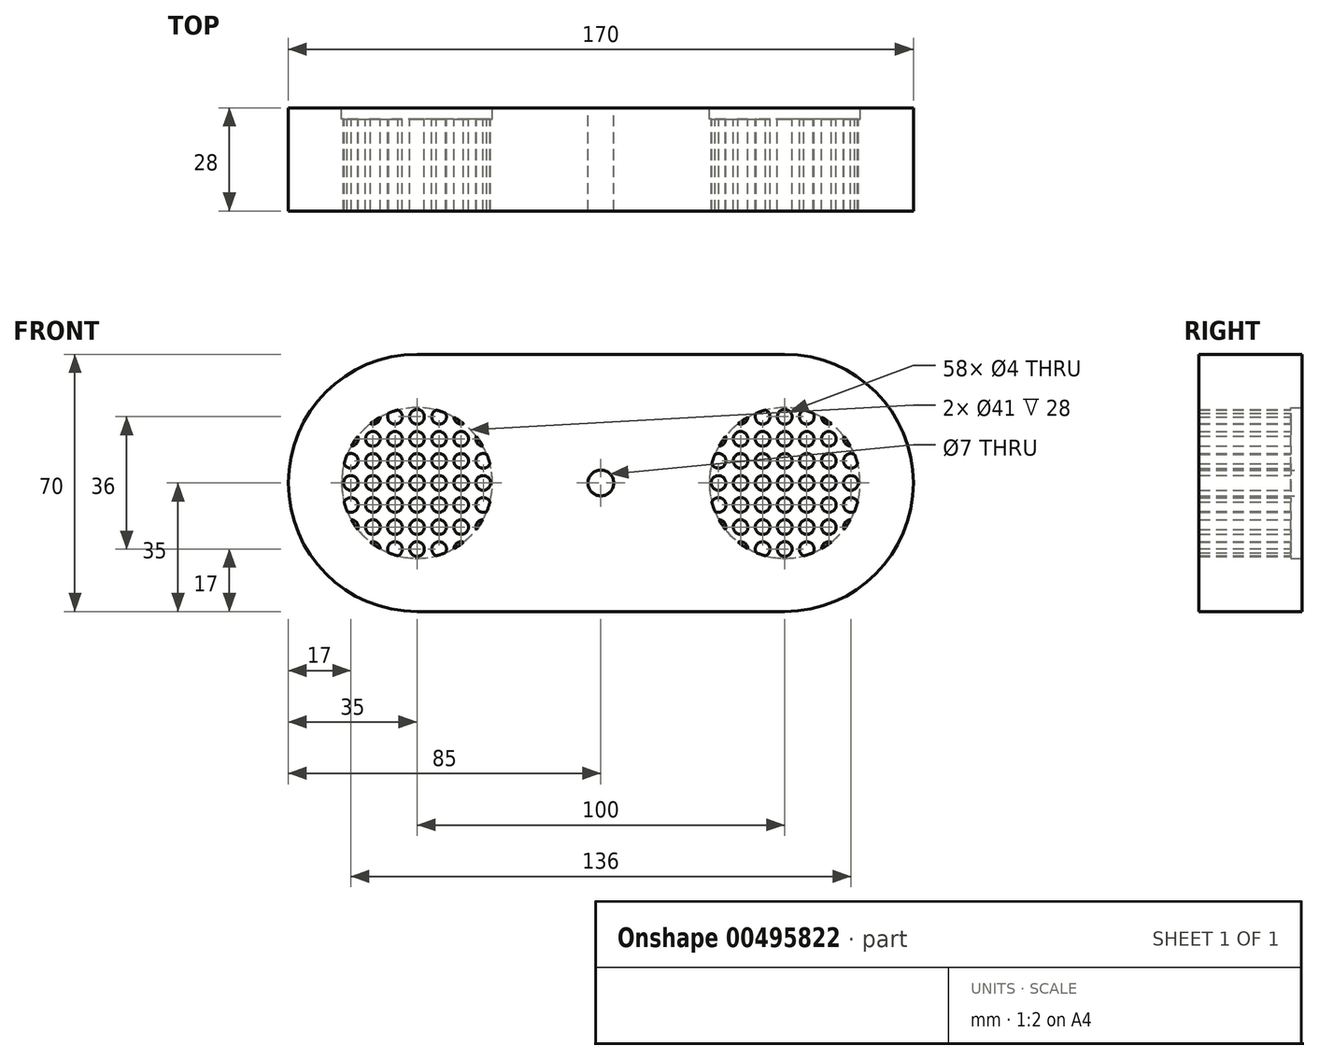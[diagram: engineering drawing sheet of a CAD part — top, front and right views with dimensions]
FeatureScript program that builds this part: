
annotation { "Feature Type Name" : "Feature", "Feature Type Description" : "" }
export const myFeature = defineFeature(function(context is Context, id is Id, definition is map)
    precondition{}
    {
        {
            var Q0;
            Q0=qCreatedBy(makeId("Front.planeOp"),FACE);
            var sketch = newSketch(context, id + "F0", { "sketchPlane" : qUnion([Q0])});
            skCircle(sketch, "E0", {"center": v(-50, 0) * mm, "radius": 20.5 * mm});
            skLineSegment(sketch, "E1", {"start": v(-50, -35) * mm, "end": v(50, -35) * mm});
            skArc(sketch, "E2", {"start": v(50, -35) * mm, "mid": v(85, 0) * mm, "end": v(50, 35) * mm});
            skLineSegment(sketch, "E3", {"start": v(50, 35) * mm, "end": v(-50, 35) * mm});
            skArc(sketch, "E4", {"start": v(-50, 35) * mm, "mid": v(-85, 0) * mm, "end": v(-50, -35) * mm});
            skCircle(sketch, "E5", {"center": v(50, 0) * mm, "radius": 20.5 * mm});
            skCircle(sketch, "E6", {"center": v(0, 0) * mm, "radius": 3.5 * mm});
            skSolve(sketch);
        }
        {
            var Q0;
            Q0 = qSketchRegion(id + "F0", true);
            extrude(context, id + "F1", {"entities" : qUnion([Q0]), "depth" : 3 * mm, "offsetDistance" : 25 * mm});
        }
        {
            var Q0;
            Q0=makeQuery(id+"F1.opExtrude","CAP_FACE",FACE,{"disambiguationData":[OSD([sQuery(id+"F0.wireOp",EDGE,"E0"),sQuery(id+"F0.wireOp",EDGE,"E1"),sQuery(id+"F0.wireOp",EDGE,"E2"),sQuery(id+"F0.wireOp",EDGE,"E3"),sQuery(id+"F0.wireOp",EDGE,"E4"),sQuery(id+"F0.wireOp",EDGE,"E5"),sQuery(id+"F0.wireOp",EDGE,"E6")])],"isStart":false});
            var sketch = newSketch(context, id + "F2", { "sketchPlane" : qUnion([Q0])});
            skLineSegment(sketch, "E7", {"start": v(-50, 0) * mm, "end": v(-29.5, 0) * mm, "construction": true});
            skLineSegment(sketch, "E8", {"start": v(-50, 0) * mm, "end": v(-70.5, 0) * mm, "construction": true});
            skCircle(sketch, "E9", {"center": v(-50, 0) * mm, "radius": 2 * mm});
            skCircle(sketch, "E10.1.0.0", {"center": v(-44, 0) * mm, "radius": 2 * mm});
            skCircle(sketch, "E10.2.0.0", {"center": v(-38, 0) * mm, "radius": 2 * mm});
            skCircle(sketch, "E10.3.0.0", {"center": v(-32, 0) * mm, "radius": 2 * mm});
            skLineSegment(sketch, "E10.direction1", {"start": v(-50, 0) * mm, "end": v(-44, 0) * mm, "construction": true});
            skCircle(sketch, "E11.0.1.0", {"center": v(-50, 6) * mm, "radius": 2 * mm});
            skLineSegment(sketch, "E11.0.1.1", {"start": v(-50, 6) * mm, "end": v(-29.5, 6) * mm, "construction": true});
            skCircle(sketch, "E11.0.1.2", {"center": v(-44, 6) * mm, "radius": 2 * mm});
            skCircle(sketch, "E11.0.1.3", {"center": v(-38, 6) * mm, "radius": 2 * mm});
            skArc(sketch, "E11.0.1.4", {"start": v(-31.02, 7.74) * mm, "mid": v(-33.9, 5.37) * mm, "end": v(-30.17, 5.2) * mm});
            skLineSegment(sketch, "E11.0.1.5", {"start": v(-50, 6) * mm, "end": v(-44, 6) * mm, "construction": true});
            skCircle(sketch, "E11.0.2.0", {"center": v(-50, 12) * mm, "radius": 2 * mm});
            skLineSegment(sketch, "E11.0.2.1", {"start": v(-50, 12) * mm, "end": v(-29.5, 12) * mm, "construction": true});
            skCircle(sketch, "E11.0.2.2", {"center": v(-44, 12) * mm, "radius": 2 * mm});
            skCircle(sketch, "E11.0.2.3", {"center": v(-38, 12) * mm, "radius": 2 * mm});
            skArc(sketch, "E11.0.2.4", {"start": v(-33.88, 12.67) * mm, "mid": v(-33.66, 10.9) * mm, "end": v(-32.1, 10) * mm});
            skLineSegment(sketch, "E11.0.2.5", {"start": v(-50, 12) * mm, "end": v(-44, 12) * mm, "construction": true});
            skLineSegment(sketch, "E11.direction1", {"start": v(-50, 0) * mm, "end": v(-25, 0) * mm, "construction": true});
            skLineSegment(sketch, "E11.direction2", {"start": v(-50, 0) * mm, "end": v(-50, 6) * mm, "construction": true});
            skCircle(sketch, "E12.0.0.3", {"center": v(-50, 18) * mm, "radius": 2 * mm});
            skLineSegment(sketch, "E12.2.0.3", {"start": v(-50, 18) * mm, "end": v(-29.5, 18) * mm, "construction": true});
            skArc(sketch, "E12.5.0.3", {"start": v(-44.8, 19.83) * mm, "mid": v(-44.63, 16.1) * mm, "end": v(-42.26, 18.98) * mm});
            skArc(sketch, "E12.7.0.3", {"start": v(-40, 18) * mm, "mid": v(-39.15, 16.37) * mm, "end": v(-37.33, 16.12) * mm});
            skLineSegment(sketch, "E12.11.0.3", {"start": v(-50, 18) * mm, "end": v(-44, 18) * mm, "construction": true});
            skArc(sketch, "E13.MirrorC", {"start": v(-40, -18) * mm, "mid": v(-39.15, -16.37) * mm, "end": v(-37.33, -16.12) * mm});
            skLineSegment(sketch, "E14.MirrorCS", {"start": v(-50, -18) * mm, "end": v(-44, -18) * mm, "construction": true});
            skLineSegment(sketch, "E15.MirrorCS", {"start": v(-50, -12) * mm, "end": v(-29.5, -12) * mm, "construction": true});
            skCircle(sketch, "E16.MirrorC", {"center": v(-44, -12) * mm, "radius": 2 * mm});
            skCircle(sketch, "E17.MirrorC", {"center": v(-50, -6) * mm, "radius": 2 * mm});
            skLineSegment(sketch, "E18.MirrorCS", {"start": v(-50, -6) * mm, "end": v(-29.5, -6) * mm, "construction": true});
            skCircle(sketch, "E19.MirrorC", {"center": v(-44, -6) * mm, "radius": 2 * mm});
            skLineSegment(sketch, "E20.MirrorCS", {"start": v(-50, -6) * mm, "end": v(-44, -6) * mm, "construction": true});
            skCircle(sketch, "E21.MirrorC", {"center": v(-38, -6) * mm, "radius": 2 * mm});
            skArc(sketch, "E22.MirrorC", {"start": v(-31.02, -7.74) * mm, "mid": v(-33.9, -5.37) * mm, "end": v(-30.17, -5.2) * mm});
            skCircle(sketch, "E23.MirrorC", {"center": v(-50, -12) * mm, "radius": 2 * mm});
            skArc(sketch, "E24.MirrorC", {"start": v(-33.88, -12.67) * mm, "mid": v(-33.66, -10.9) * mm, "end": v(-32.1, -10) * mm});
            skArc(sketch, "E25.MirrorC", {"start": v(-44.8, -19.83) * mm, "mid": v(-44.63, -16.1) * mm, "end": v(-42.26, -18.98) * mm});
            skLineSegment(sketch, "E26.MirrorCS", {"start": v(-50, -12) * mm, "end": v(-44, -12) * mm, "construction": true});
            skLineSegment(sketch, "E27.MirrorCS", {"start": v(-50, -18) * mm, "end": v(-29.5, -18) * mm, "construction": true});
            skCircle(sketch, "E28.MirrorC", {"center": v(-38, -12) * mm, "radius": 2 * mm});
            skCircle(sketch, "E29.MirrorC", {"center": v(-50, -18) * mm, "radius": 2 * mm});
            skCircle(sketch, "E30.MirrorC", {"center": v(-56, 6) * mm, "radius": 2 * mm});
            skCircle(sketch, "E31.MirrorC", {"center": v(-56, 0) * mm, "radius": 2 * mm});
            skCircle(sketch, "E32.MirrorC", {"center": v(-62, -12) * mm, "radius": 2 * mm});
            skArc(sketch, "E33.MirrorC", {"start": v(-60, -17.9) * mm, "mid": v(-60.9, -16.34) * mm, "end": v(-62.67, -16.12) * mm});
            skCircle(sketch, "E34.MirrorC", {"center": v(-62, 0) * mm, "radius": 2 * mm});
            skArc(sketch, "E35.MirrorC", {"start": v(-55.2, 19.83) * mm, "mid": v(-55.37, 16.1) * mm, "end": v(-57.74, 18.98) * mm});
            skArc(sketch, "E36.MirrorC", {"start": v(-66.12, -12.67) * mm, "mid": v(-66.34, -10.9) * mm, "end": v(-67.9, -10) * mm});
            skCircle(sketch, "E37.MirrorC", {"center": v(-62, -6) * mm, "radius": 2 * mm});
            skArc(sketch, "E38.MirrorC", {"start": v(-68.98, 7.74) * mm, "mid": v(-66.1, 5.37) * mm, "end": v(-69.83, 5.2) * mm});
            skCircle(sketch, "E39.MirrorC", {"center": v(-68, 0) * mm, "radius": 2 * mm});
            skArc(sketch, "E40.MirrorC", {"start": v(-66.12, 12.67) * mm, "mid": v(-66.34, 10.9) * mm, "end": v(-67.9, 10) * mm});
            skCircle(sketch, "E41.MirrorC", {"center": v(-62, 6) * mm, "radius": 2 * mm});
            skCircle(sketch, "E42.MirrorC", {"center": v(-56, 12) * mm, "radius": 2 * mm});
            skCircle(sketch, "E43.MirrorC", {"center": v(-56, -6) * mm, "radius": 2 * mm});
            skCircle(sketch, "E44.MirrorC", {"center": v(-56, -12) * mm, "radius": 2 * mm});
            skArc(sketch, "E45.MirrorC", {"start": v(-55.2, -19.83) * mm, "mid": v(-55.37, -16.1) * mm, "end": v(-57.74, -18.98) * mm});
            skArc(sketch, "E46.MirrorC", {"start": v(-68.98, -7.74) * mm, "mid": v(-66.1, -5.37) * mm, "end": v(-69.83, -5.2) * mm});
            skArc(sketch, "E47.MirrorC", {"start": v(-60, 17.9) * mm, "mid": v(-60.9, 16.34) * mm, "end": v(-62.67, 16.12) * mm});
            skCircle(sketch, "E48.MirrorC", {"center": v(-62, 12) * mm, "radius": 2 * mm});
            skCircle(sketch, "E49", {"center": v(-50, 0) * mm, "radius": 20.5 * mm});
            skArc(sketch, "E50.MirrorCS", {"start": v(60, 17.9) * mm, "mid": v(60.9, 16.34) * mm, "end": v(62.67, 16.12) * mm});
            skArc(sketch, "E51.MirrorCS", {"start": v(33.88, -12.67) * mm, "mid": v(33.66, -10.9) * mm, "end": v(32.1, -10) * mm});
            skArc(sketch, "E52.MirrorCS", {"start": v(60, -17.9) * mm, "mid": v(60.9, -16.34) * mm, "end": v(62.67, -16.12) * mm});
            skArc(sketch, "E53.MirrorCS", {"start": v(66.12, 12.67) * mm, "mid": v(66.34, 10.9) * mm, "end": v(67.9, 10) * mm});
            skArc(sketch, "E54.MirrorCS", {"start": v(44.8, -19.83) * mm, "mid": v(44.63, -16.1) * mm, "end": v(42.26, -18.98) * mm});
            skLineSegment(sketch, "E55.MirrorCS", {"start": v(50, -18) * mm, "end": v(44, -18) * mm, "construction": true});
            skLineSegment(sketch, "E56.MirrorCS", {"start": v(50, -12) * mm, "end": v(44, -12) * mm, "construction": true});
            skArc(sketch, "E57.MirrorCS", {"start": v(40, -18) * mm, "mid": v(39.15, -16.37) * mm, "end": v(37.33, -16.12) * mm});
            skLineSegment(sketch, "E58.MirrorCS", {"start": v(50, 0) * mm, "end": v(44, 0) * mm, "construction": true});
            skArc(sketch, "E59.MirrorCS", {"start": v(40, 18) * mm, "mid": v(39.15, 16.37) * mm, "end": v(37.33, 16.12) * mm});
            skLineSegment(sketch, "E60.MirrorCS", {"start": v(50, 0) * mm, "end": v(29.5, 0) * mm, "construction": true});
            skArc(sketch, "E61.MirrorCS", {"start": v(33.88, 12.67) * mm, "mid": v(33.66, 10.9) * mm, "end": v(32.1, 10) * mm});
            skArc(sketch, "E62.MirrorCS", {"start": v(66.12, -12.67) * mm, "mid": v(66.34, -10.9) * mm, "end": v(67.9, -10) * mm});
            skLineSegment(sketch, "E63.MirrorCS", {"start": v(50, 0) * mm, "end": v(50, 6) * mm, "construction": true});
            skCircle(sketch, "E64.MirrorC", {"center": v(62, 12) * mm, "radius": 2 * mm});
            skCircle(sketch, "E65.MirrorC", {"center": v(56, 0) * mm, "radius": 2 * mm});
            skCircle(sketch, "E66.MirrorC", {"center": v(50, -6) * mm, "radius": 2 * mm});
            skCircle(sketch, "E67.MirrorC", {"center": v(50, 18) * mm, "radius": 2 * mm});
            skLineSegment(sketch, "E68.MirrorCS", {"start": v(50, -12) * mm, "end": v(29.5, -12) * mm, "construction": true});
            skCircle(sketch, "E69.MirrorC", {"center": v(50, 0) * mm, "radius": 20.5 * mm});
            skLineSegment(sketch, "E70.MirrorCS", {"start": v(50, -6) * mm, "end": v(29.5, -6) * mm, "construction": true});
            skCircle(sketch, "E71.MirrorC", {"center": v(62, 6) * mm, "radius": 2 * mm});
            skLineSegment(sketch, "E72.MirrorCS", {"start": v(50, 18) * mm, "end": v(29.5, 18) * mm, "construction": true});
            skCircle(sketch, "E73.MirrorC", {"center": v(62, 0) * mm, "radius": 2 * mm});
            skArc(sketch, "E74.MirrorCS", {"start": v(55.2, 19.83) * mm, "mid": v(55.37, 16.1) * mm, "end": v(57.74, 18.98) * mm});
            skCircle(sketch, "E75.MirrorC", {"center": v(56, 12) * mm, "radius": 2 * mm});
            skArc(sketch, "E76.MirrorCS", {"start": v(44.8, 19.83) * mm, "mid": v(44.63, 16.1) * mm, "end": v(42.26, 18.98) * mm});
            skCircle(sketch, "E77.MirrorC", {"center": v(50, 12) * mm, "radius": 2 * mm});
            skArc(sketch, "E78.MirrorCS", {"start": v(68.98, 7.74) * mm, "mid": v(66.1, 5.37) * mm, "end": v(69.83, 5.2) * mm});
            skLineSegment(sketch, "E79.MirrorCS", {"start": v(50, 0) * mm, "end": v(25, 0) * mm, "construction": true});
            skArc(sketch, "E80.MirrorCS", {"start": v(31.02, -7.74) * mm, "mid": v(33.9, -5.37) * mm, "end": v(30.17, -5.2) * mm});
            skCircle(sketch, "E81.MirrorC", {"center": v(62, -12) * mm, "radius": 2 * mm});
            skCircle(sketch, "E82.MirrorC", {"center": v(50, -18) * mm, "radius": 2 * mm});
            skArc(sketch, "E83.MirrorCS", {"start": v(55.2, -19.83) * mm, "mid": v(55.37, -16.1) * mm, "end": v(57.74, -18.98) * mm});
            skCircle(sketch, "E84.MirrorC", {"center": v(38, 6) * mm, "radius": 2 * mm});
            skCircle(sketch, "E85.MirrorC", {"center": v(68, 0) * mm, "radius": 2 * mm});
            skCircle(sketch, "E86.MirrorC", {"center": v(44, -6) * mm, "radius": 2 * mm});
            skLineSegment(sketch, "E87.MirrorCS", {"start": v(50, 12) * mm, "end": v(44, 12) * mm, "construction": true});
            skCircle(sketch, "E88.MirrorC", {"center": v(38, -6) * mm, "radius": 2 * mm});
            skArc(sketch, "E89.MirrorCS", {"start": v(31.02, 7.74) * mm, "mid": v(33.9, 5.37) * mm, "end": v(30.17, 5.2) * mm});
            skLineSegment(sketch, "E90.MirrorCS", {"start": v(50, 18) * mm, "end": v(44, 18) * mm, "construction": true});
            skCircle(sketch, "E91.MirrorC", {"center": v(44, 0) * mm, "radius": 2 * mm});
            skCircle(sketch, "E92.MirrorC", {"center": v(38, 0) * mm, "radius": 2 * mm});
            skLineSegment(sketch, "E93.MirrorCS", {"start": v(50, 6) * mm, "end": v(44, 6) * mm, "construction": true});
            skCircle(sketch, "E94.MirrorC", {"center": v(50, -12) * mm, "radius": 2 * mm});
            skCircle(sketch, "E95.MirrorC", {"center": v(38, -12) * mm, "radius": 2 * mm});
            skCircle(sketch, "E96.MirrorC", {"center": v(56, -12) * mm, "radius": 2 * mm});
            skCircle(sketch, "E97.MirrorC", {"center": v(50, 0) * mm, "radius": 2 * mm});
            skCircle(sketch, "E98.MirrorC", {"center": v(38, 12) * mm, "radius": 2 * mm});
            skLineSegment(sketch, "E99.MirrorCS", {"start": v(50, -18) * mm, "end": v(29.5, -18) * mm, "construction": true});
            skCircle(sketch, "E100.MirrorC", {"center": v(50, 6) * mm, "radius": 2 * mm});
            skCircle(sketch, "E101.MirrorC", {"center": v(32, 0) * mm, "radius": 2 * mm});
            skLineSegment(sketch, "E102.MirrorCS", {"start": v(50, -6) * mm, "end": v(44, -6) * mm, "construction": true});
            skCircle(sketch, "E103.MirrorC", {"center": v(56, -6) * mm, "radius": 2 * mm});
            skCircle(sketch, "E104.MirrorC", {"center": v(62, -6) * mm, "radius": 2 * mm});
            skCircle(sketch, "E105.MirrorC", {"center": v(56, 6) * mm, "radius": 2 * mm});
            skLineSegment(sketch, "E106.MirrorCS", {"start": v(50, 0) * mm, "end": v(70.5, 0) * mm, "construction": true});
            skCircle(sketch, "E107.MirrorC", {"center": v(44, 6) * mm, "radius": 2 * mm});
            skLineSegment(sketch, "E108.MirrorCS", {"start": v(50, 12) * mm, "end": v(29.5, 12) * mm, "construction": true});
            skArc(sketch, "E109.MirrorCS", {"start": v(68.98, -7.74) * mm, "mid": v(66.1, -5.37) * mm, "end": v(69.83, -5.2) * mm});
            skLineSegment(sketch, "E110.MirrorCS", {"start": v(50, 6) * mm, "end": v(29.5, 6) * mm, "construction": true});
            skCircle(sketch, "E111.MirrorC", {"center": v(44, 12) * mm, "radius": 2 * mm});
            skCircle(sketch, "E112.MirrorC", {"center": v(44, -12) * mm, "radius": 2 * mm});
            skSolve(sketch);
        }
        {
            var Q0;
            Q0=makeQuery(id+"F2.imprint","IMPRINT",FACE,{"disambiguationData":[TD([[makeQuery(id+"F2.imprint","IMPRINT",EDGE,{"derivedFrom":sQuery(id+"F2.wireOp",EDGE,"E9")}),-1.0]])]});
            var Q1;
            Q1=makeQuery(id+"F2.imprint","IMPRINT",FACE,{"disambiguationData":[TD([[makeQuery(id+"F2.imprint","IMPRINT",EDGE,{"derivedFrom":makeQuery(id+"F1.opExtrude","CAP_EDGE",EDGE,{"disambiguationData":[OSD([sQuery(id+"F0.wireOp",EDGE,"E1")])],"isStart":false})}),1.0]])]});
            var Q2;
            {var subQ5=sQuery(id+"F2.wireOp",EDGE,"E50.MirrorCS");Q2=makeQuery(id+"F2.imprint","IMPRINT",FACE,{"disambiguationData":[TD([[makeQuery(id+"F2.imprint","IMPRINT",EDGE,{"derivedFrom":subQ5}),-1.0]])]});}
            extrude(context, id + "F3", {"entities" : qUnion([Q0, Q1, Q2]), "operationType" : NewBodyOperationType.ADD, "depth" : 25 * mm, "offsetDistance" : 25 * mm});
        }
    });
